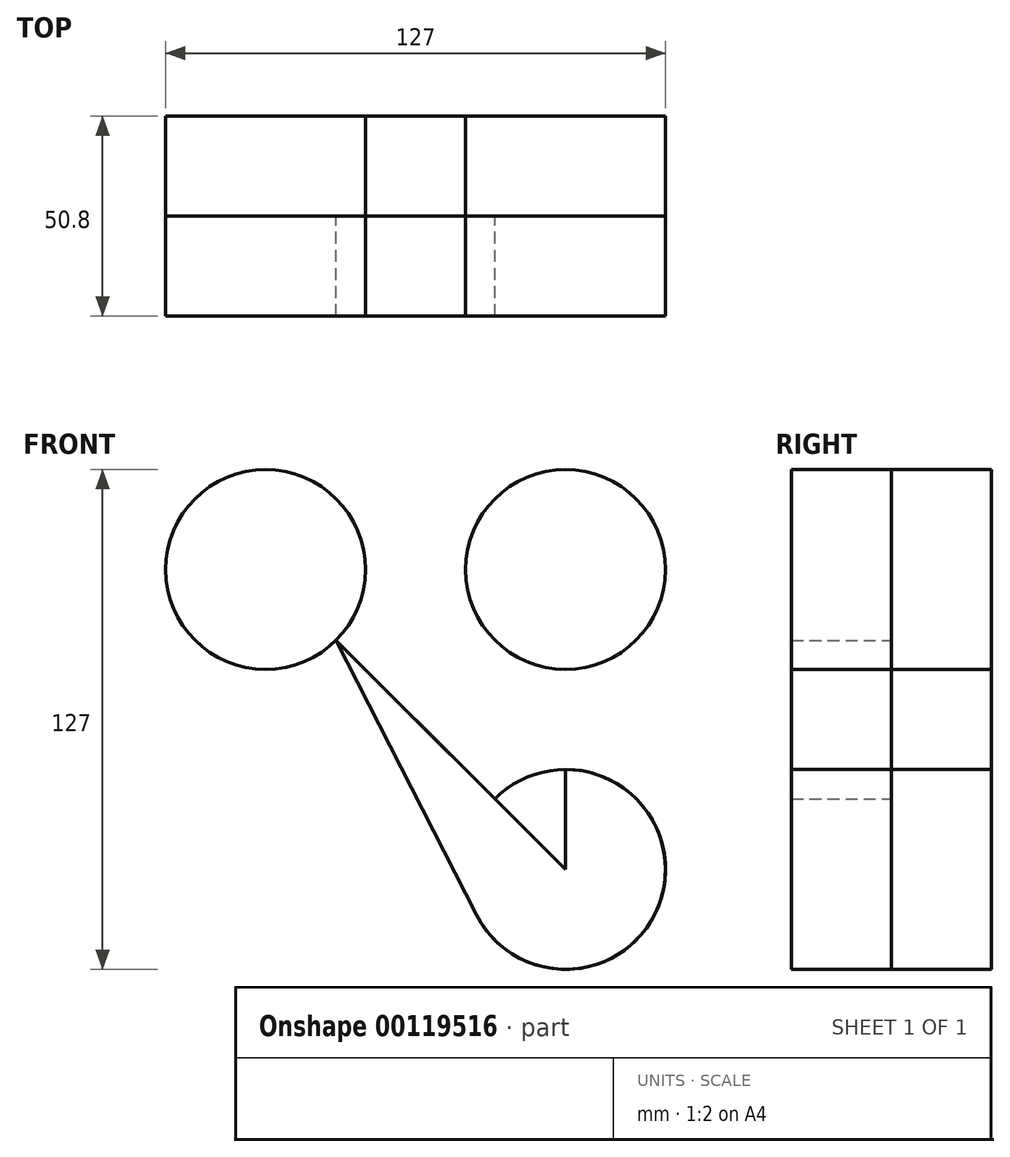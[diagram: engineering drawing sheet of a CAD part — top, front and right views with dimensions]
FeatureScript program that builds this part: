
annotation { "Feature Type Name" : "Feature", "Feature Type Description" : "" }
export const myFeature = defineFeature(function(context is Context, id is Id, definition is map)
    precondition{}
    {
        {
            var Q0;
            Q0=qCreatedBy(makeId("Front.planeOp"),FACE);
            var sketch = newSketch(context, id + "F0", { "sketchPlane" : qUnion([Q0])});
            skCircle(sketch, "E0", {"center": v(0, 0) * mm, "radius": 25.4 * mm});
            skCircle(sketch, "E1", {"center": v(0, 76.2) * mm, "radius": 25.4 * mm});
            skCircle(sketch, "E2", {"center": v(-76.2, 76.2) * mm, "radius": 25.4 * mm});
            skLineSegment(sketch, "E3", {"start": v(0, 0) * mm, "end": v(-76.2, 76.2) * mm});
            skLineSegment(sketch, "E4", {"start": v(0, 76.2) * mm, "end": v(-76.2, 76.2) * mm, "construction": true});
            skLineSegment(sketch, "E5", {"start": v(0, 76.2) * mm, "end": v(0, 0) * mm});
            skLineSegment(sketch, "E6", {"start": v(-58.24, 58.24) * mm, "end": v(-22.62, -11.55) * mm});
            skSolve(sketch);
        }
        {
            var Q0;
            Q0 = qSketchRegion(id + "F0", true);
            extrude(context, id + "F1", {"entities" : qUnion([Q0]), "depth" : 25.4 * mm});
        }
        {
            var Q0;
            Q0=makeQuery(id+"F0.imprint","IMPRINT",FACE,{"disambiguationData":[TD([[makeQuery(id+"F0.imprint","IMPRINT",EDGE,{"derivedFrom":sQuery(id+"F0.wireOp",EDGE,"E2")}),1.0]])]});
            var Q1;
            {var subQ0=sQuery(id+"F0.wireOp",EDGE,"E6");Q1=makeQuery(id+"F0.imprint","IMPRINT",FACE,{"disambiguationData":[TD([[makeQuery(id+"F0.imprint","IMPRINT",EDGE,{"derivedFrom":subQ0}),1.0]])]});}
            var Q2;
            {var subQ0=sQuery(id+"F0.wireOp",EDGE,"E0");var subQ1=makeQuery(id+"F0.imprint","INTERSECT",VERTEX,{"derivedFrom":[subQ0,sQuery(id+"F0.wireOp",EDGE,"E6")]});Q2=makeQuery(id+"F0.imprint","IMPRINT",FACE,{"disambiguationData":[TD([[makeQuery(id+"F0.imprint","IMPRINT",EDGE,{"disambiguationData":[TD([[subQ1,1.0]])],"derivedFrom":subQ0}),1.0]])]});}
            var Q3;
            Q3=makeQuery(id+"F0.imprint","IMPRINT",FACE,{"disambiguationData":[TD([[makeQuery(id+"F0.imprint","IMPRINT",EDGE,{"derivedFrom":sQuery(id+"F0.wireOp",EDGE,"E1")}),1.0]])]});
            extrude(context, id + "F2", {"entities" : qUnion([Q0, Q1, Q2, Q3]), "endBound" : BoundingType.SYMMETRIC, "depth" : 50.8 * mm});
        }
    });
